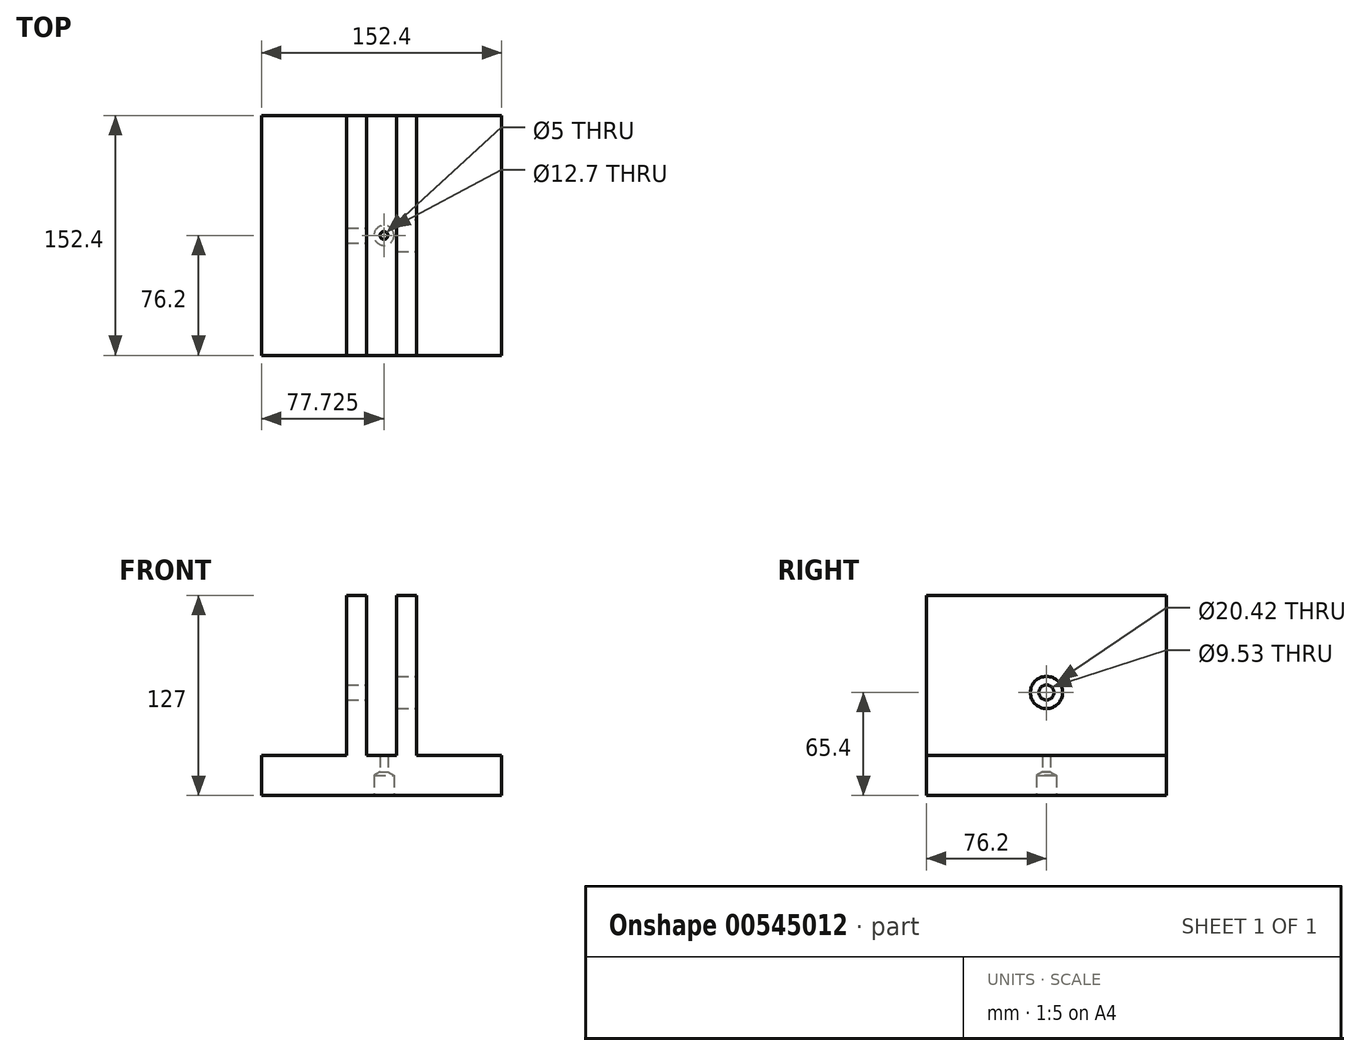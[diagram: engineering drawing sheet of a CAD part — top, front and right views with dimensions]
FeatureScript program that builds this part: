
annotation { "Feature Type Name" : "Feature", "Feature Type Description" : "" }
export const myFeature = defineFeature(function(context is Context, id is Id, definition is map)
    precondition{}
    {
        {
            var Q0;
            Q0=qCreatedBy(makeId("Top.planeOp"),FACE);
            var sketch = newSketch(context, id + "F0", { "sketchPlane" : qUnion([Q0])});
            skLineSegment(sketch, "E0.bottom", {"start": v(76.2, 76.2) * mm, "end": v(-76.2, 76.2) * mm});
            skLineSegment(sketch, "E0.top", {"start": v(76.2, -76.2) * mm, "end": v(-76.2, -76.2) * mm});
            skLineSegment(sketch, "E0.left", {"start": v(76.2, 76.2) * mm, "end": v(76.2, -76.2) * mm});
            skLineSegment(sketch, "E0.right", {"start": v(-76.2, 76.2) * mm, "end": v(-76.2, -76.2) * mm});
            skPoint(sketch, "E0.middle", {"position": v(0, 0) * mm});
            skSolve(sketch);
        }
        {
            var Q0;
            Q0 = qSketchRegion(id + "F0", true);
            extrude(context, id + "F1", {"entities" : qUnion([Q0]), "depth" : 25.4 * mm, "offsetDistance" : 25.4 * mm});
        }
        {
            var Q0;
            Q0=makeQuery(id+"F1.opExtrude","CAP_FACE",FACE,{"disambiguationData":[OSD([sQuery(id+"F0.wireOp",EDGE,"E0.bottom"),sQuery(id+"F0.wireOp",EDGE,"E0.top"),sQuery(id+"F0.wireOp",EDGE,"E0.left"),sQuery(id+"F0.wireOp",EDGE,"E0.right")])],"isStart":false});
            var sketch = newSketch(context, id + "F2", { "sketchPlane" : qUnion([Q0])});
            skLineSegment(sketch, "E1", {"start": v(0, 0) * mm, "end": v(0, -76.2) * mm, "construction": true});
            skLineSegment(sketch, "E2", {"start": v(9.53, -76.2) * mm, "end": v(-9.52, -76.2) * mm, "construction": true});
            skLineSegment(sketch, "E3", {"start": v(0, 0) * mm, "end": v(0, 76.2) * mm, "construction": true});
            skLineSegment(sketch, "E4", {"start": v(22.22, 76.2) * mm, "end": v(-22.23, 76.2) * mm, "construction": true});
            skLineSegment(sketch, "E5.bottom", {"start": v(-9.52, -76.2) * mm, "end": v(-22.23, -76.2) * mm});
            skLineSegment(sketch, "E5.top", {"start": v(-9.52, 76.2) * mm, "end": v(-22.23, 76.2) * mm});
            skLineSegment(sketch, "E5.left", {"start": v(-9.52, -76.2) * mm, "end": v(-9.52, 76.2) * mm});
            skLineSegment(sketch, "E5.right", {"start": v(-22.23, -76.2) * mm, "end": v(-22.23, 76.2) * mm});
            skLineSegment(sketch, "E6.bottom", {"start": v(9.53, -76.2) * mm, "end": v(22.22, -76.2) * mm});
            skLineSegment(sketch, "E6.top", {"start": v(9.53, 76.2) * mm, "end": v(22.22, 76.2) * mm});
            skLineSegment(sketch, "E6.left", {"start": v(9.53, -76.2) * mm, "end": v(9.53, 76.2) * mm});
            skLineSegment(sketch, "E6.right", {"start": v(22.22, -76.2) * mm, "end": v(22.22, 76.2) * mm});
            skSolve(sketch);
        }
        {
            var Q0;
            Q0 = qSketchRegion(id + "F2", true);
            extrude(context, id + "F3", {"entities" : qUnion([Q0]), "operationType" : NewBodyOperationType.ADD, "depth" : 101.6 * mm, "offsetDistance" : 25.4 * mm});
        }
        {
            var Q0;
            Q0=makeQuery(id+"F3.opExtrude","SWEPT_FACE",FACE,{"disambiguationData":[OSD([sQuery(id+"F2.wireOp",EDGE,"E6.right")])]});
            var sketch = newSketch(context, id + "F4", { "sketchPlane" : qUnion([Q0])});
            skLineSegment(sketch, "E7", {"start": v(0, 25.4) * mm, "end": v(0, 65.4) * mm, "construction": true});
            skCircle(sketch, "E8", {"center": v(0, 65.4) * mm, "radius": 10.21 * mm});
            skSolve(sketch);
        }
        {
            var Q0;
            Q0=sQuery(id+"F4.wireOp",VERTEX,"E7.end");
            var Q1;
            Q1=makeQuery(id+"F1.opExtrude","SWEPT_BODY",BODY,{"disambiguationData":[OSD([sQuery(id+"F0.wireOp",EDGE,"E0.bottom"),sQuery(id+"F0.wireOp",EDGE,"E0.top"),sQuery(id+"F0.wireOp",EDGE,"E0.left"),sQuery(id+"F0.wireOp",EDGE,"E0.right")])]});
            hole(context, id + "F5", {"style" : HoleStyle.SIMPLE, "endStyle" : HoleEndStyle.BLIND, "holeDiameter" : 20.42 * mm, "holeDepth" : 12.7 * mm, "isTappedThrough" : true, "tappedDepth" : 12.7 * mm, "tapClearance" : 3, "locations" : qUnion([Q0]), "scope" : qUnion([Q1])});
        }
        {
            var Q0;
            Q0=makeQuery(id+"F1.opExtrude","CAP_FACE",FACE,{"disambiguationData":[OSD([sQuery(id+"F0.wireOp",EDGE,"E0.bottom"),sQuery(id+"F0.wireOp",EDGE,"E0.top"),sQuery(id+"F0.wireOp",EDGE,"E0.left"),sQuery(id+"F0.wireOp",EDGE,"E0.right")])],"isStart":true});
            var sketch = newSketch(context, id + "F6", { "sketchPlane" : qUnion([Q0])});
            skPoint(sketch, "E9", {"position": v(1.53, 0) * mm});
            skSolve(sketch);
        }
        {
            var Q0;
            Q0=sQuery(id+"F6.wireOp",VERTEX,"E9");
            var Q1;
            Q1=makeQuery(id+"F1.opExtrude","SWEPT_BODY",BODY,{"disambiguationData":[OSD([sQuery(id+"F0.wireOp",EDGE,"E0.bottom"),sQuery(id+"F0.wireOp",EDGE,"E0.top"),sQuery(id+"F0.wireOp",EDGE,"E0.left"),sQuery(id+"F0.wireOp",EDGE,"E0.right")])]});
            hole(context, id + "F7", {"style" : HoleStyle.SIMPLE, "endStyle" : HoleEndStyle.BLIND, "holeDiameter" : 5 * mm, "holeDepth" : 25.4 * mm, "isTappedThrough" : true, "tappedDepth" : 12.7 * mm, "tapClearance" : 3, "locations" : qUnion([Q0]), "scope" : qUnion([Q1])});
        }
        {
            var Q0;
            Q0=sQuery(id+"F6.wireOp",VERTEX,"E9");
            var Q1;
            Q1=makeQuery(id+"F1.opExtrude","SWEPT_BODY",BODY,{"disambiguationData":[OSD([sQuery(id+"F0.wireOp",EDGE,"E0.bottom"),sQuery(id+"F0.wireOp",EDGE,"E0.top"),sQuery(id+"F0.wireOp",EDGE,"E0.left"),sQuery(id+"F0.wireOp",EDGE,"E0.right")])]});
            hole(context, id + "F8", {"style" : HoleStyle.SIMPLE, "endStyle" : HoleEndStyle.BLIND, "holeDiameter" : 12.7 * mm, "holeDepth" : 12.7 * mm, "isTappedThrough" : true, "tappedDepth" : 12.7 * mm, "tapClearance" : 3, "locations" : qUnion([Q0]), "scope" : qUnion([Q1])});
        }
        {
            var Q0;
            Q0=sQuery(id+"F4.wireOp",VERTEX,"E8.center");
            var Q1;
            Q1=makeQuery(id+"F1.opExtrude","SWEPT_BODY",BODY,{"disambiguationData":[OSD([sQuery(id+"F0.wireOp",EDGE,"E0.bottom"),sQuery(id+"F0.wireOp",EDGE,"E0.top"),sQuery(id+"F0.wireOp",EDGE,"E0.left"),sQuery(id+"F0.wireOp",EDGE,"E0.right")])]});
            hole(context, id + "F9", {"style" : HoleStyle.SIMPLE, "endStyle" : HoleEndStyle.BLIND, "holeDiameter" : 9.52 * mm, "holeDepth" : 44.45 * mm, "isTappedThrough" : true, "tappedDepth" : 12.7 * mm, "tapClearance" : 3, "locations" : qUnion([Q0]), "scope" : qUnion([Q1])});
        }
    });
